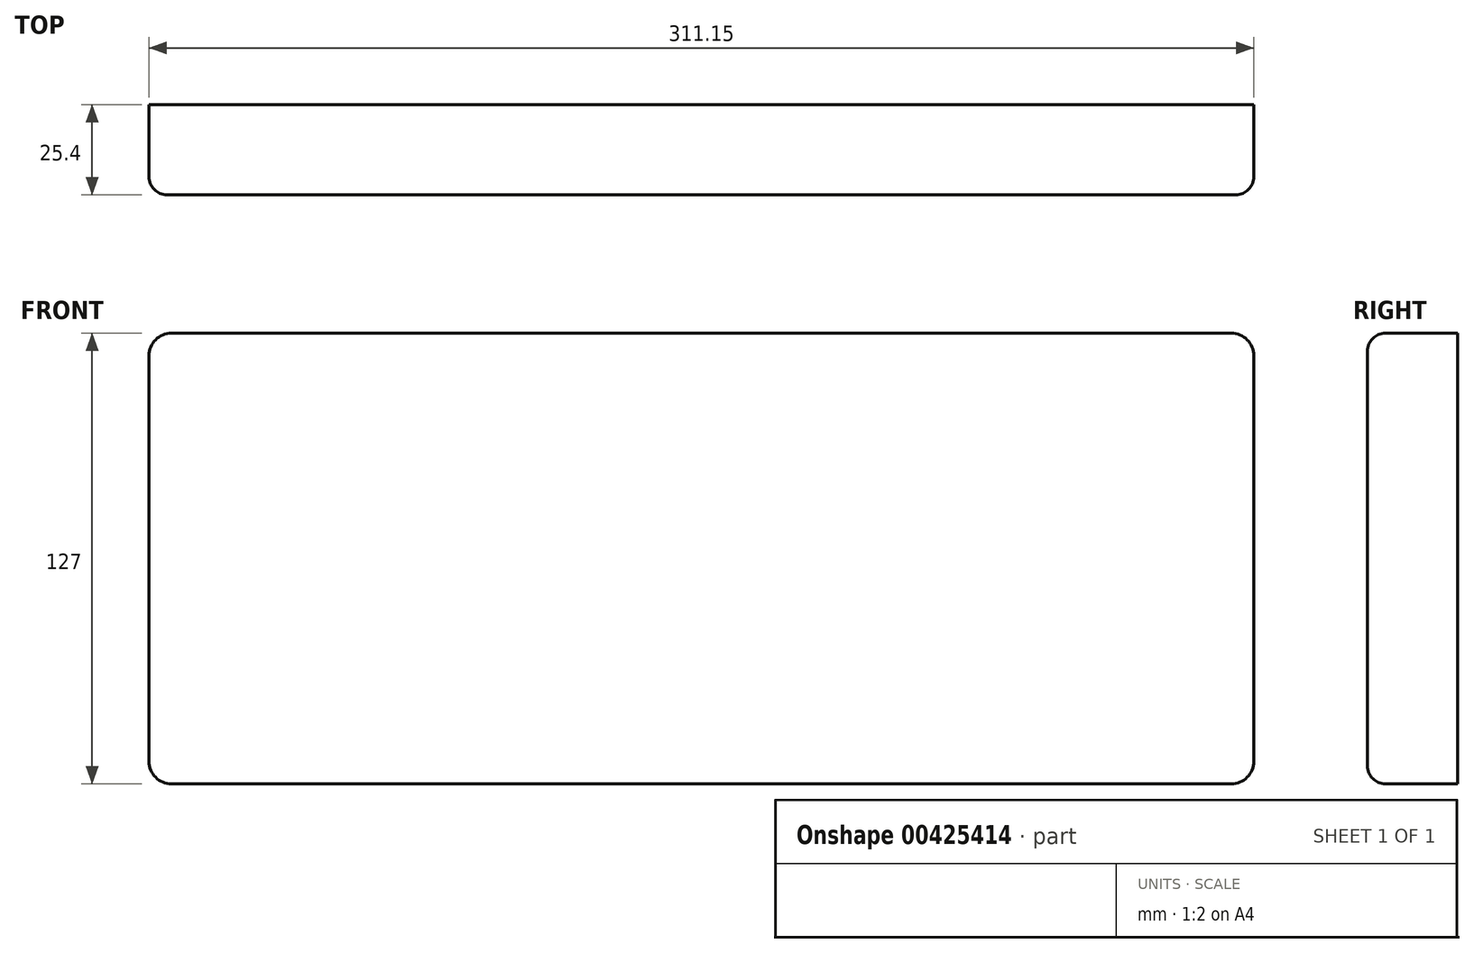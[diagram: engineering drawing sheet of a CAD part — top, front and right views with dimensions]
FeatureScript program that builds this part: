
annotation { "Feature Type Name" : "Feature", "Feature Type Description" : "" }
export const myFeature = defineFeature(function(context is Context, id is Id, definition is map)
    precondition{}
    {
        {
            var Q0;
            Q0=qCreatedBy(makeId("Front.planeOp"),FACE);
            var sketch = newSketch(context, id + "F0", { "sketchPlane" : qUnion([Q0])});
            skLineSegment(sketch, "E0.bottom", {"start": v(6.35, 0) * mm, "end": v(304.8, 0) * mm});
            skLineSegment(sketch, "E0.top", {"start": v(6.35, 127) * mm, "end": v(304.8, 127) * mm});
            skLineSegment(sketch, "E0.left", {"start": v(0, 6.35) * mm, "end": v(0, 120.65) * mm});
            skLineSegment(sketch, "E0.right", {"start": v(311.15, 6.35) * mm, "end": v(311.15, 120.65) * mm});
            skPoint(sketch, "E1.visualSharp", {"position": v(0, 127) * mm});
            skArc(sketch, "E1.filletArc", {"start": v(6.35, 127) * mm, "mid": v(1.86, 125.14) * mm, "end": v(0, 120.65) * mm});
            skPoint(sketch, "E2.visualSharp", {"position": v(311.15, 127) * mm});
            skArc(sketch, "E2.filletArc", {"start": v(311.15, 120.65) * mm, "mid": v(309.3, 125.14) * mm, "end": v(304.8, 127) * mm});
            skPoint(sketch, "E3.visualSharp", {"position": v(311.15, 0) * mm});
            skArc(sketch, "E3.filletArc", {"start": v(304.8, 0) * mm, "mid": v(309.3, 1.86) * mm, "end": v(311.15, 6.35) * mm});
            skPoint(sketch, "E4.visualSharp", {"position": v(0, 0) * mm});
            skArc(sketch, "E4.filletArc", {"start": v(0, 6.35) * mm, "mid": v(1.86, 1.86) * mm, "end": v(6.35, 0) * mm});
            skSolve(sketch);
        }
        {
            var Q0;
            Q0=makeQuery(id+"F0.imprint","IMPRINT",FACE,{"disambiguationData":[TD([[makeQuery(id+"F0.imprint","IMPRINT",EDGE,{"derivedFrom":sQuery(id+"F0.wireOp",EDGE,"E0.bottom")}),1.0]])]});
            extrude(context, id + "F1", {"entities" : qUnion([Q0]), "depth" : 25.4 * mm});
        }
        {
            var Q0;
            Q0=makeQuery(id+"F1.opExtrude","CAP_EDGE",EDGE,{"disambiguationData":[OSD([sQuery(id+"F0.wireOp",EDGE,"E0.top")])],"isStart":false});
            var Q1;
            Q1=makeQuery(id+"F1.opExtrude","CAP_EDGE",EDGE,{"disambiguationData":[OSD([sQuery(id+"F0.wireOp",EDGE,"E0.right")])],"isStart":false});
            var Q2;
            Q2=makeQuery(id+"F1.opExtrude","CAP_EDGE",EDGE,{"disambiguationData":[OSD([sQuery(id+"F0.wireOp",EDGE,"E0.bottom")])],"isStart":false});
            var Q3;
            Q3=makeQuery(id+"F1.opExtrude","CAP_EDGE",EDGE,{"disambiguationData":[OSD([sQuery(id+"F0.wireOp",EDGE,"E0.left")])],"isStart":false});
            fillet(context, id + "F2", {"entities" : qUnion([Q0, Q1, Q2, Q3]), "radius" : 5.08 * mm, "tangentPropagation" : true, "allowEdgeOverflow" : false});
        }
    });
